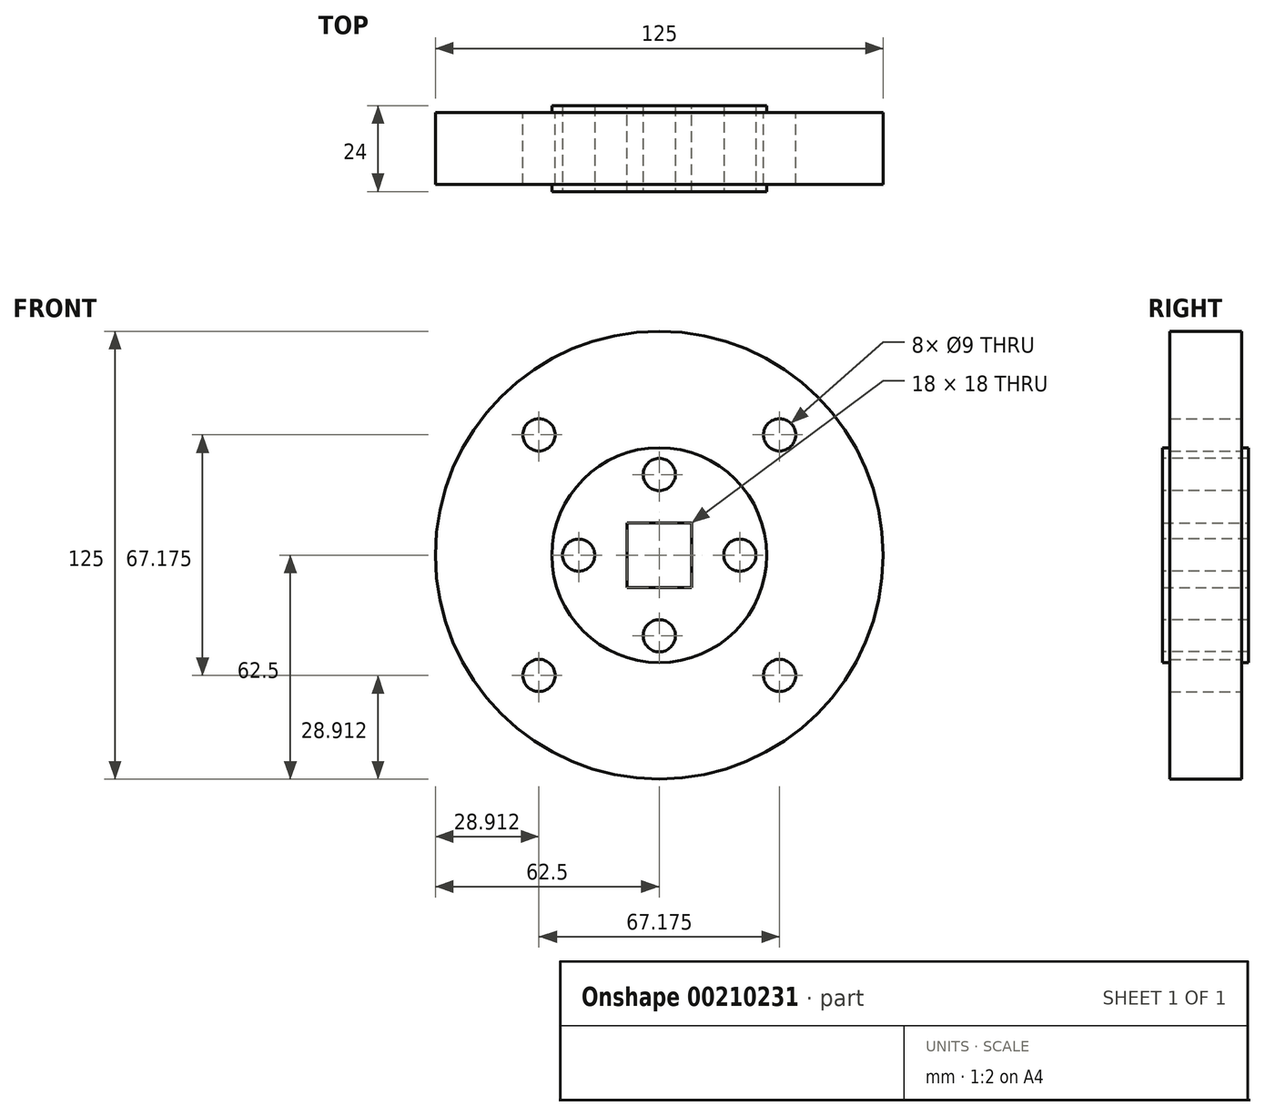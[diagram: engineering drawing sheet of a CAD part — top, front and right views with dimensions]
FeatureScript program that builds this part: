
annotation { "Feature Type Name" : "Feature", "Feature Type Description" : "" }
export const myFeature = defineFeature(function(context is Context, id is Id, definition is map)
    precondition{}
    {
        {
            var Q0;
            Q0=qCreatedBy(makeId("Front.planeOp"),FACE);
            var sketch = newSketch(context, id + "F0", { "sketchPlane" : qUnion([Q0])});
            skCircle(sketch, "E0", {"center": v(0, 0) * mm, "radius": 62.5 * mm});
            skLineSegment(sketch, "E1.bottom", {"start": v(61.75, 63.25) * mm, "end": v(-61.75, 63.25) * mm, "construction": true});
            skLineSegment(sketch, "E1.top", {"start": v(61.75, -63.25) * mm, "end": v(-61.75, -63.25) * mm, "construction": true});
            skLineSegment(sketch, "E1.left", {"start": v(61.75, 63.25) * mm, "end": v(61.75, -63.25) * mm, "construction": true});
            skLineSegment(sketch, "E1.right", {"start": v(-61.75, 63.25) * mm, "end": v(-61.75, -63.25) * mm, "construction": true});
            skCircle(sketch, "E2", {"center": v(0, 0) * mm, "radius": 47.5 * mm, "construction": true});
            skLineSegment(sketch, "E3", {"start": v(0, 0) * mm, "end": v(33.59, -33.59) * mm, "construction": true});
            skLineSegment(sketch, "E4", {"start": v(0, 0) * mm, "end": v(-33.59, -33.59) * mm, "construction": true});
            skLineSegment(sketch, "E5", {"start": v(0, 0) * mm, "end": v(-33.59, 33.59) * mm, "construction": true});
            skLineSegment(sketch, "E6", {"start": v(0, 0) * mm, "end": v(33.59, 33.59) * mm, "construction": true});
            skCircle(sketch, "E7", {"center": v(-33.59, 33.59) * mm, "radius": 4.5 * mm});
            skCircle(sketch, "E8", {"center": v(33.59, 33.59) * mm, "radius": 4.5 * mm});
            skCircle(sketch, "E9", {"center": v(33.59, -33.59) * mm, "radius": 4.5 * mm});
            skCircle(sketch, "E10", {"center": v(-33.59, -33.59) * mm, "radius": 4.5 * mm});
            skLineSegment(sketch, "E11.bottom", {"start": v(-9, 9) * mm, "end": v(9, 9) * mm});
            skLineSegment(sketch, "E11.top", {"start": v(-9, -9) * mm, "end": v(9, -9) * mm});
            skLineSegment(sketch, "E11.left", {"start": v(-9, 9) * mm, "end": v(-9, -9) * mm});
            skLineSegment(sketch, "E11.right", {"start": v(9, 9) * mm, "end": v(9, -9) * mm});
            skSolve(sketch);
        }
        {
            var Q0;
            Q0 = qSketchRegion(id + "F0", true);
            extrude(context, id + "F1", {"entities" : qUnion([Q0]), "depth" : 20 * mm});
        }
        {
            var Q0;
            Q0=makeQuery(id+"F1.opExtrude","CAP_FACE",FACE,{"disambiguationData":[OSD([sQuery(id+"F0.wireOp",EDGE,"E0"),sQuery(id+"F0.wireOp",EDGE,"E7"),sQuery(id+"F0.wireOp",EDGE,"E8"),sQuery(id+"F0.wireOp",EDGE,"E9"),sQuery(id+"F0.wireOp",EDGE,"E10"),sQuery(id+"F0.wireOp",EDGE,"E11.bottom"),sQuery(id+"F0.wireOp",EDGE,"E11.top"),sQuery(id+"F0.wireOp",EDGE,"E11.left"),sQuery(id+"F0.wireOp",EDGE,"E11.right")])],"isStart":false});
            var sketch = newSketch(context, id + "F2", { "sketchPlane" : qUnion([Q0])});
            skCircle(sketch, "E12", {"center": v(0, 0) * mm, "radius": 30 * mm});
            skLineSegment(sketch, "E13.bottom", {"start": v(-9, 9) * mm, "end": v(9, 9) * mm});
            skLineSegment(sketch, "E13.top", {"start": v(-9, -9) * mm, "end": v(9, -9) * mm});
            skLineSegment(sketch, "E13.left", {"start": v(-9, 9) * mm, "end": v(-9, -9) * mm});
            skLineSegment(sketch, "E13.right", {"start": v(9, 9) * mm, "end": v(9, -9) * mm});
            skSolve(sketch);
        }
        {
            var Q0;
            Q0 = qSketchRegion(id + "F2", true);
            extrude(context, id + "F3", {"entities" : qUnion([Q0]), "operationType" : NewBodyOperationType.ADD, "depth" : 2 * mm});
        }
        {
            var Q0;
            Q0=makeQuery(id+"F1.opExtrude","CAP_FACE",FACE,{"disambiguationData":[OSD([sQuery(id+"F0.wireOp",EDGE,"E0"),sQuery(id+"F0.wireOp",EDGE,"E7"),sQuery(id+"F0.wireOp",EDGE,"E8"),sQuery(id+"F0.wireOp",EDGE,"E9"),sQuery(id+"F0.wireOp",EDGE,"E10"),sQuery(id+"F0.wireOp",EDGE,"E11.bottom"),sQuery(id+"F0.wireOp",EDGE,"E11.top"),sQuery(id+"F0.wireOp",EDGE,"E11.left"),sQuery(id+"F0.wireOp",EDGE,"E11.right")])],"isStart":true});
            var sketch = newSketch(context, id + "F4", { "sketchPlane" : qUnion([Q0])});
            skCircle(sketch, "E14", {"center": v(0, 0) * mm, "radius": 30 * mm});
            skLineSegment(sketch, "E15.bottom", {"start": v(-9, 9) * mm, "end": v(9, 9) * mm});
            skLineSegment(sketch, "E15.top", {"start": v(-9, -9) * mm, "end": v(9, -9) * mm});
            skLineSegment(sketch, "E15.left", {"start": v(-9, 9) * mm, "end": v(-9, -9) * mm});
            skLineSegment(sketch, "E15.right", {"start": v(9, 9) * mm, "end": v(9, -9) * mm});
            skSolve(sketch);
        }
        {
            var Q0;
            Q0 = qSketchRegion(id + "F4", true);
            extrude(context, id + "F5", {"entities" : qUnion([Q0]), "operationType" : NewBodyOperationType.ADD, "depth" : 2 * mm});
        }
        {
            var Q0;
            Q0=makeQuery(id+"F3.opExtrude","CAP_FACE",FACE,{"disambiguationData":[OSD([sQuery(id+"F2.wireOp",EDGE,"E12"),sQuery(id+"F2.wireOp",EDGE,"E13.bottom"),sQuery(id+"F2.wireOp",EDGE,"E13.top"),sQuery(id+"F2.wireOp",EDGE,"E13.left"),sQuery(id+"F2.wireOp",EDGE,"E13.right")])],"isStart":false});
            var sketch = newSketch(context, id + "F6", { "sketchPlane" : qUnion([Q0])});
            skCircle(sketch, "E16", {"center": v(0, 0) * mm, "radius": 22.5 * mm, "construction": true});
            skLineSegment(sketch, "E17", {"start": v(0, 30) * mm, "end": v(0, -30) * mm, "construction": true});
            skLineSegment(sketch, "E18", {"start": v(-30, 0) * mm, "end": v(30, 0) * mm, "construction": true});
            skCircle(sketch, "E19", {"center": v(0, 22.5) * mm, "radius": 4.5 * mm});
            skCircle(sketch, "E20", {"center": v(22.5, 0) * mm, "radius": 4.5 * mm});
            skCircle(sketch, "E21", {"center": v(0, -22.5) * mm, "radius": 4.5 * mm});
            skCircle(sketch, "E22", {"center": v(-22.5, 0) * mm, "radius": 4.5 * mm});
            skSolve(sketch);
        }
        {
            var Q0;
            Q0 = qSketchRegion(id + "F6", true);
            extrude(context, id + "F7", {"entities" : qUnion([Q0]), "operationType" : NewBodyOperationType.REMOVE, "oppositeDirection" : true, "depth" : 30 * mm});
        }
    });
